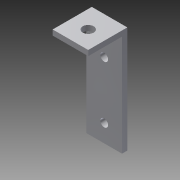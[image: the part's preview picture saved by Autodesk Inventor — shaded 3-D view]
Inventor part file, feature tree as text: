
AUTODESK INVENTOR PART (.ipt)
format: ipt  version: 2015 (Build 190159000, 159)  size: 131,584 bytes
history: native  units: mm
features: sketch x6, extrude x5, other x1, hole x1
ambient origin geometry x8: Origin, YZ Plane, XZ Plane, XY Plane, X Axis, Y Axis, Z Axis, Center Point
bodies: Body1 (feature_tree)
feature tree (13):
  other  "ソリッド1"
  extrude  "押し出し1"  Depth=10.0mm
  extrude  "押し出し2"  Depth=10.0mm
  extrude  "押し出し6"  Depth=1.0mm TaperAngle=0.0deg
  extrude  "押し出し7"  Depth=1.0mm
  extrude  "押し出し8"  Depth=30.0mm TaperAngle=0.0deg
  hole  "穴3"  [1 undecoded]
  sketch  "スケッチ1"
  sketch  "スケッチ4"
  sketch  "スケッチ9"
  sketch  "スケッチ10"
  sketch  "スケッチ11"
  sketch  "スケッチ12"
note: 1 required parameter value undecoded (feature->parameter linkage not recoverable at this tier; creation-order binding heuristic only, values carry confidence <= 0.55)
